# Revit family: Napoleon Entice™ 60 Electric Fireplace
name_source: partatom
category: Electrical Fixtures
units: mm (PartAtom-declared; Revit-internal decimal feet)

## family parameters
Always vertical = Yes
Cut with Voids When Loaded = No
Host = Wall
Maintain Annotation Orientation = No
OmniClass Number = 23.80.00.00
OmniClass Title = Electric Power and Lighting
Part Type = Normal
Room Calculation Point = No
Round Connector Dimension = Use Diameter
Shared = No

## types (1)
- Napoleon Entice™ 60 Electric Fireplace
    Area = 0
    BarCode = <None>
    Default Elevation = 0' - 0"
    Depth = 0' - 5 7/16"
    Frame Length = 4' - 11 11/16"
    Frame Width = 1' - 4 15/16"
    HandicapAccessible = Yes
    Height = 0
    IsExtendedWarranty = 0
    IsExternal = Yes
    Length = 4' - 10 7/16"
    ReplacementCost = 0
    Screen Length = 4' - 7 3/4"
    Screen Width = 0' - 11 15/16"
    WarrantyDurationLabor = 0
    WarrantyDurationParts = 0
    WarrantyPeriod = 0
    Width = 1' - 3 11/16"

## geometry (parser evidence)
native form markers: Sweep x1
no freeform markers — native parametric forms only
